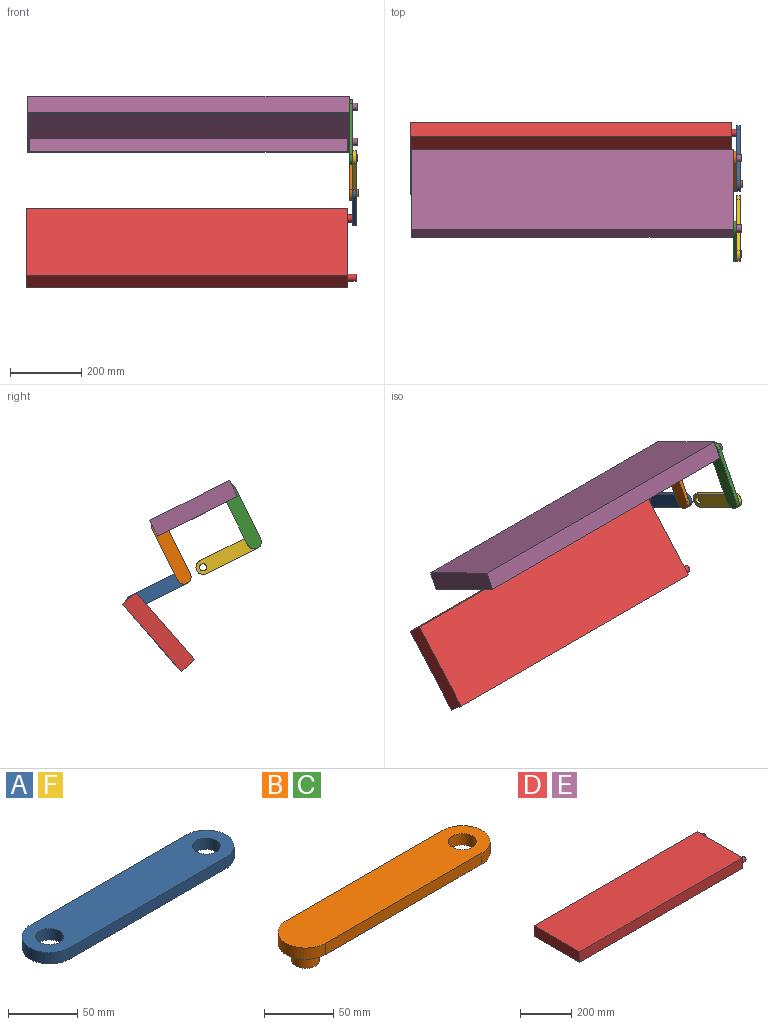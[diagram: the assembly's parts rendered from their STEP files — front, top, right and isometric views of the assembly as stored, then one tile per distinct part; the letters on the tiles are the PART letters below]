
ASSEMBLY  parts=6 mates=5
PART A: 8 faces, bbox 200x40x10 mm
  f0: plane 160x10mm, normal (0,-1,0), area 1600mm2, adj f1,f4,f5,f6
  f1: cylinder r=20mm len=40mm, axis (0,0,-1), area 628.3mm2, adj f0,f2,f5,f6
  f2: plane 160x10mm, normal (0,1,0), area 1600mm2, adj f1,f4,f5,f6
  f3: cylinder r=10mm len=20mm, axis (0,0,-1), area 628.3mm2, adj f5,f6
  f4: cylinder r=20mm len=40mm, axis (0,0,-1), area 628.3mm2, adj f0,f2,f5,f6
  f5: plane 200x40mm, normal (0,0,1), area 7028.3mm2, adj f0,f1,f2,f3,f4,f7
  f6: plane 200x40mm, normal (0,0,-1), area 7028.3mm2, adj f0,f1,f2,f3,f4,f7
  f7: cylinder r=10mm len=20mm, axis (0,0,-1), area 628.3mm2, adj f5,f6
PART B: 9 faces, bbox 200x40x25 mm
  f0: plane 160x10mm, normal (0,-1,0), area 1600mm2, adj f1,f4,f5,f6
  f1: cylinder r=20mm len=40mm, axis (0,0,-1), area 628.3mm2, adj f0,f2,f5,f6
  f2: plane 160x10mm, normal (0,1,0), area 1600mm2, adj f1,f4,f5,f6
  f3: cylinder r=10mm len=20mm, axis (0,0,-1), area 628.3mm2, adj f5,f6
  f4: cylinder r=20mm len=40mm, axis (0,0,-1), area 628.3mm2, adj f0,f2,f5,f6
  f5: plane 200x40mm, normal (0,0,1), area 7342.5mm2, adj f0,f1,f2,f3,f4
  f6: plane 200x40mm, normal (0,0,-1), area 7028.3mm2, adj f0,f1,f2,f3,f4,f7
  f7: cylinder r=10mm len=20mm, axis (0,0,1), area 942.5mm2, adj f6,f8
  f8: plane 20x20mm, normal (0,0,-1), area 314.2mm2, adj f7
PART C: same geometry as B
PART D: 15 faces, bbox 925x250x50 mm
  f0: plane 890x40mm, normal (0,-1,0), area 35600mm2, adj f1,f3,f9,f10
  f1: plane 240x40mm, normal (-1,0,0), area 9600mm2, adj f0,f2,f9,f10
  f2: plane 890x40mm, normal (0,1,0), area 35600mm2, adj f1,f3,f9,f10
  f3: plane 240x40mm, normal (1,0,0), area 9600mm2, adj f0,f2,f9,f10
  f4: plane 250x50mm, normal (1,0,0), area 11871.7mm2, adj f5,f7,f8,f9,f11,f13
  f5: plane 900x50mm, normal (0,1,0), area 45000mm2, adj f4,f6,f8,f9
  f6: plane 250x50mm, normal (-1,0,0), area 12500mm2, adj f5,f7,f8,f9
  f7: plane 900x50mm, normal (0,-1,0), area 45000mm2, adj f4,f6,f8,f9
  f8: plane 900x250mm, normal (0,0,1), area 225000mm2, adj f4,f5,f6,f7
  f9: plane 900x250mm, normal (0,0,-1), area 11400mm2, adj f0,f1,f2,f3,f4,f5,f6,f7
  f10: plane 890x240mm, normal (0,0,-1), area 213600mm2, adj f0,f1,f2,f3
  f11: cylinder r=10mm len=25mm, axis (-1,0,0), area 1570.8mm2, adj f4,f12
  f12: plane 20x20mm, normal (1,0,0), area 314.2mm2, adj f11
  f13: cylinder r=10mm len=25mm, axis (-1,0,0), area 1570.8mm2, adj f4,f14
  f14: plane 20x20mm, normal (1,0,0), area 314.2mm2, adj f13
PART E: same geometry as D
PART F: same geometry as A
PLACE A rot(axis=(0.47,-0.75,-0.47),106.1deg) t=(606.59,-390.68,1289.44)mm
PLACE B rot(axis=(-0.22,-0.95,0.22),93deg) t=(260.59,731.58,1219.47)mm
PLACE C rot(axis=(-0.22,-0.95,0.22),93deg) t=(260.59,534.77,1317.79)mm
PLACE D rot(axis=(1,0,0),49deg) t=(-204.41,117.94,486.6)mm
PLACE E rot(axis=(-1,0,0),26.5deg) t=(-199.41,-9.92,827.44)mm
PLACE F rot(axis=(0.47,-0.75,-0.47),106.1deg) t=(606.59,-587.48,1387.76)mm
MATE revolute F.f1 <-> C.f4  axis (-1,0,0) through (260.59,-168.66,755.84)mm
MATE revolute B.f1 <-> E.f13  axis (-1,0,0) through (250.59,99.65,800.64)mm
MATE revolute C.f1 <-> E.f11  axis (-1,0,0) through (250.59,-97.15,898.97)mm
MATE revolute A.f1 <-> B.f4  axis (-1,0,0) through (260.59,28.14,657.51)mm
MATE revolute A.f4 <-> D.f13  axis (1,0,0) through (270.59,171.27,586)mm
